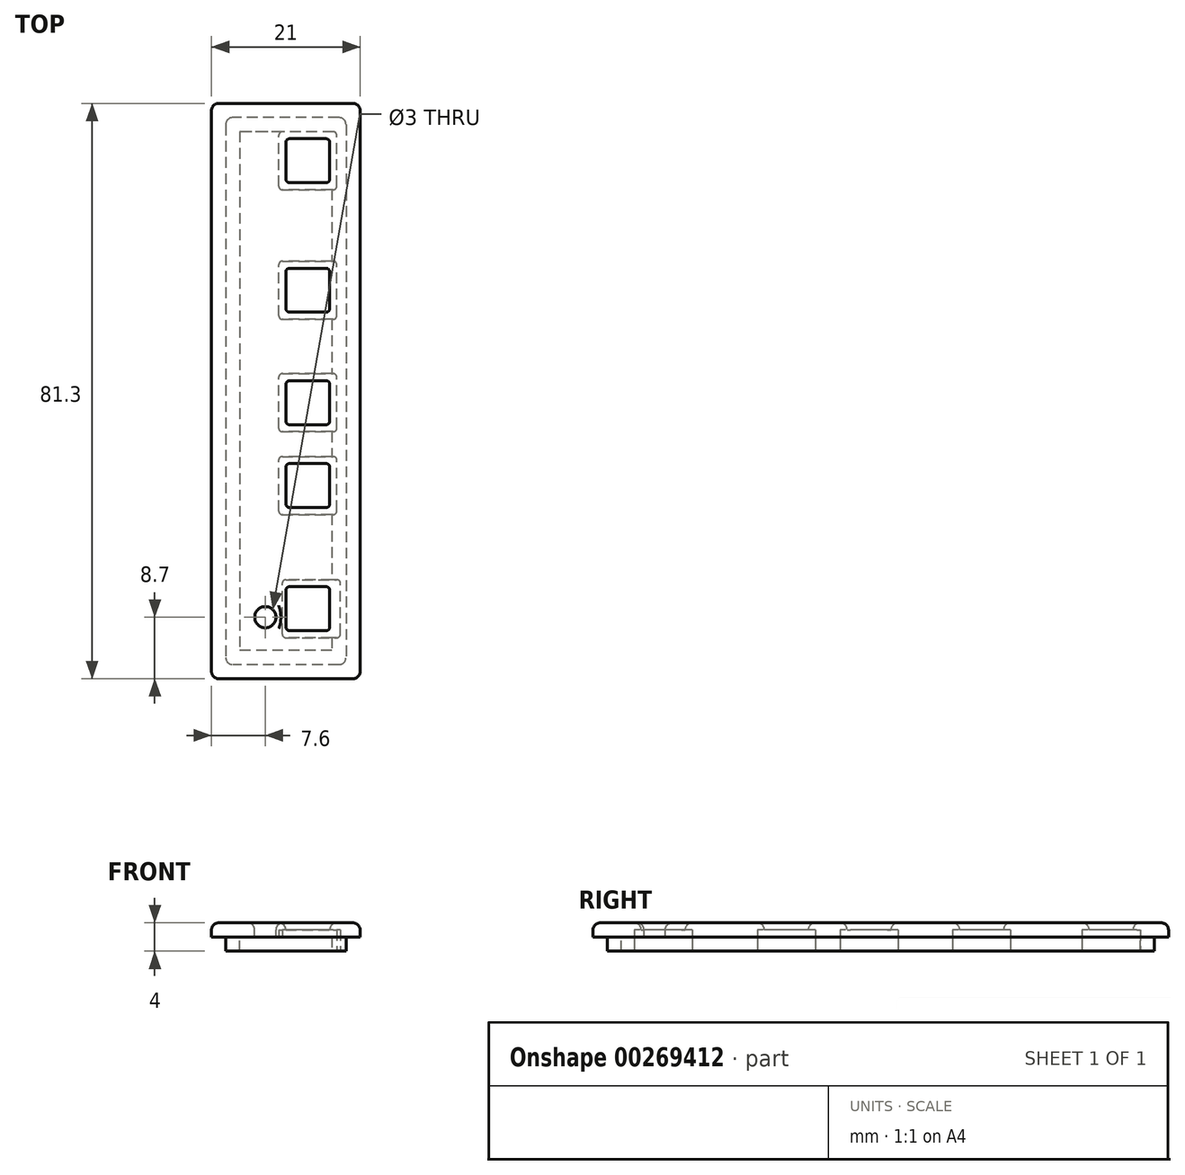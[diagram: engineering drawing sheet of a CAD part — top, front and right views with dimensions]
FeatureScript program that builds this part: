
annotation { "Feature Type Name" : "Feature", "Feature Type Description" : "" }
export const myFeature = defineFeature(function(context is Context, id is Id, definition is map)
    precondition{}
    {
        {
            var Q0;
            Q0=qCreatedBy(makeId("Top.planeOp"),FACE);
            var sketch = newSketch(context, id + "F0", { "sketchPlane" : qUnion([Q0])});
            skLineSegment(sketch, "E0.bottom", {"start": v(8.5, 38.65) * mm, "end": v(-8.5, 38.65) * mm});
            skLineSegment(sketch, "E0.top", {"start": v(8.5, -38.65) * mm, "end": v(-8.5, -38.65) * mm});
            skLineSegment(sketch, "E0.left", {"start": v(8.5, 38.65) * mm, "end": v(8.5, -38.65) * mm});
            skLineSegment(sketch, "E0.right", {"start": v(-8.5, 38.65) * mm, "end": v(-8.5, -38.65) * mm});
            skPoint(sketch, "E0.middle", {"position": v(0, 0) * mm});
            skLineSegment(sketch, "E1.0", {"start": v(10.5, 40.65) * mm, "end": v(-10.5, 40.65) * mm});
            skLineSegment(sketch, "E1.1", {"start": v(10.5, 40.65) * mm, "end": v(10.5, -40.65) * mm});
            skLineSegment(sketch, "E1.2", {"start": v(10.5, -40.65) * mm, "end": v(-10.5, -40.65) * mm});
            skLineSegment(sketch, "E1.3", {"start": v(-10.5, 40.65) * mm, "end": v(-10.5, -40.65) * mm});
            skLineSegment(sketch, "E2.0", {"start": v(6.5, 36.65) * mm, "end": v(-6.5, 36.65) * mm});
            skLineSegment(sketch, "E2.1", {"start": v(6.5, 36.65) * mm, "end": v(6.5, -36.65) * mm});
            skLineSegment(sketch, "E2.2", {"start": v(6.5, -36.65) * mm, "end": v(-6.5, -36.65) * mm});
            skLineSegment(sketch, "E2.3", {"start": v(-6.5, 36.65) * mm, "end": v(-6.5, -36.65) * mm});
            skSolve(sketch);
        }
        {
            var Q0;
            Q0=makeQuery(id+"F0.imprint","IMPRINT",FACE,{"disambiguationData":[TD([[makeQuery(id+"F0.imprint","IMPRINT",EDGE,{"derivedFrom":sQuery(id+"F0.wireOp",EDGE,"E2.0")}),1.0]])]});
            var Q1;
            Q1=makeQuery(id+"F0.imprint","IMPRINT",FACE,{"disambiguationData":[TD([[makeQuery(id+"F0.imprint","IMPRINT",EDGE,{"derivedFrom":sQuery(id+"F0.wireOp",EDGE,"E0.bottom")}),1.0]])]});
            var Q2;
            Q2=makeQuery(id+"F0.imprint","IMPRINT",FACE,{"disambiguationData":[TD([[makeQuery(id+"F0.imprint","IMPRINT",EDGE,{"derivedFrom":sQuery(id+"F0.wireOp",EDGE,"E0.bottom")}),-1.0]])]});
            extrude(context, id + "F1", {"entities" : qUnion([Q0, Q1, Q2]), "depth" : 2 * mm});
        }
        {
            var Q0;
            Q0=makeQuery(id+"F0.imprint","IMPRINT",FACE,{"disambiguationData":[TD([[makeQuery(id+"F0.imprint","IMPRINT",EDGE,{"derivedFrom":sQuery(id+"F0.wireOp",EDGE,"E0.bottom")}),1.0]])]});
            extrude(context, id + "F2", {"entities" : qUnion([Q0]), "operationType" : NewBodyOperationType.ADD, "oppositeDirection" : true, "depth" : 2 * mm});
        }
        {
            var Q0;
            Q0=makeQuery(id+"F1.opExtrude","CAP_FACE",FACE,{"disambiguationData":[OSD([sQuery(id+"F0.wireOp",EDGE,"E1.0"),sQuery(id+"F0.wireOp",EDGE,"E1.1"),sQuery(id+"F0.wireOp",EDGE,"E1.2"),sQuery(id+"F0.wireOp",EDGE,"E1.3")])],"isStart":false});
            var sketch = newSketch(context, id + "F3", { "sketchPlane" : qUnion([Q0])});
            skLineSegment(sketch, "E3.bottom", {"start": v(5.7, 35.65) * mm, "end": v(0.5, 35.65) * mm});
            skLineSegment(sketch, "E3.top", {"start": v(5.7, 29.45) * mm, "end": v(0.5, 29.45) * mm});
            skLineSegment(sketch, "E3.left", {"start": v(6.2, 35.15) * mm, "end": v(6.2, 29.95) * mm});
            skLineSegment(sketch, "E3.right", {"start": v(0, 35.15) * mm, "end": v(0, 29.95) * mm});
            skLineSegment(sketch, "E4.bottom", {"start": v(5.7, 17.35) * mm, "end": v(0.5, 17.35) * mm});
            skLineSegment(sketch, "E4.top", {"start": v(5.7, 11.15) * mm, "end": v(0.5, 11.15) * mm});
            skLineSegment(sketch, "E4.left", {"start": v(6.2, 16.85) * mm, "end": v(6.2, 11.65) * mm});
            skLineSegment(sketch, "E4.right", {"start": v(0, 16.85) * mm, "end": v(0, 11.65) * mm});
            skLineSegment(sketch, "E5.bottom", {"start": v(0.5, 1.45) * mm, "end": v(5.7, 1.45) * mm});
            skLineSegment(sketch, "E5.top", {"start": v(0.5, -4.75) * mm, "end": v(5.7, -4.75) * mm});
            skLineSegment(sketch, "E5.left", {"start": v(0, 0.95) * mm, "end": v(0, -4.25) * mm});
            skLineSegment(sketch, "E5.right", {"start": v(6.2, 0.95) * mm, "end": v(6.2, -4.25) * mm});
            skLineSegment(sketch, "E6.bottom", {"start": v(5.7, -10.25) * mm, "end": v(0.5, -10.25) * mm});
            skLineSegment(sketch, "E6.top", {"start": v(5.7, -16.45) * mm, "end": v(0.5, -16.45) * mm});
            skLineSegment(sketch, "E6.left", {"start": v(6.2, -10.75) * mm, "end": v(6.2, -15.95) * mm});
            skLineSegment(sketch, "E6.right", {"start": v(0, -10.75) * mm, "end": v(0, -15.95) * mm});
            skLineSegment(sketch, "E7.bottom", {"start": v(5.7, -27.65) * mm, "end": v(0.5, -27.65) * mm});
            skLineSegment(sketch, "E7.top", {"start": v(5.7, -33.85) * mm, "end": v(0.5, -33.85) * mm});
            skLineSegment(sketch, "E7.left", {"start": v(6.2, -28.15) * mm, "end": v(6.2, -33.35) * mm});
            skLineSegment(sketch, "E7.right", {"start": v(0, -28.15) * mm, "end": v(0, -33.35) * mm});
            skPoint(sketch, "E8.visualSharp", {"position": v(6.2, 17.35) * mm});
            skArc(sketch, "E8.filletArc", {"start": v(6.2, 16.85) * mm, "mid": v(6.05, 17.2) * mm, "end": v(5.7, 17.35) * mm});
            skPoint(sketch, "E9.visualSharp", {"position": v(0, 17.35) * mm});
            skArc(sketch, "E9.filletArc", {"start": v(0.5, 17.35) * mm, "mid": v(0.15, 17.2) * mm, "end": v(0, 16.85) * mm});
            skPoint(sketch, "E10.visualSharp", {"position": v(0, 11.15) * mm});
            skArc(sketch, "E10.filletArc", {"start": v(0, 11.65) * mm, "mid": v(0.15, 11.3) * mm, "end": v(0.5, 11.15) * mm});
            skPoint(sketch, "E11.visualSharp", {"position": v(6.2, 11.15) * mm});
            skArc(sketch, "E11.filletArc", {"start": v(5.7, 11.15) * mm, "mid": v(6.05, 11.3) * mm, "end": v(6.2, 11.65) * mm});
            skPoint(sketch, "E12.visualSharp", {"position": v(6.2, 29.45) * mm});
            skArc(sketch, "E12.filletArc", {"start": v(5.7, 29.45) * mm, "mid": v(6.05, 29.6) * mm, "end": v(6.2, 29.95) * mm});
            skPoint(sketch, "E13.visualSharp", {"position": v(6.2, 35.65) * mm});
            skArc(sketch, "E13.filletArc", {"start": v(6.2, 35.15) * mm, "mid": v(6.05, 35.5) * mm, "end": v(5.7, 35.65) * mm});
            skPoint(sketch, "E14.visualSharp", {"position": v(0, 35.65) * mm});
            skArc(sketch, "E14.filletArc", {"start": v(0.5, 35.65) * mm, "mid": v(0.15, 35.5) * mm, "end": v(0, 35.15) * mm});
            skPoint(sketch, "E15.visualSharp", {"position": v(0, 29.45) * mm});
            skArc(sketch, "E15.filletArc", {"start": v(0, 29.95) * mm, "mid": v(0.15, 29.6) * mm, "end": v(0.5, 29.45) * mm});
            skPoint(sketch, "E16.visualSharp", {"position": v(0, 1.45) * mm});
            skArc(sketch, "E16.filletArc", {"start": v(0.5, 1.45) * mm, "mid": v(0.15, 1.3) * mm, "end": v(0, 0.95) * mm});
            skPoint(sketch, "E17.visualSharp", {"position": v(0, -4.75) * mm});
            skArc(sketch, "E17.filletArc", {"start": v(0, -4.25) * mm, "mid": v(0.15, -4.6) * mm, "end": v(0.5, -4.75) * mm});
            skPoint(sketch, "E18.visualSharp", {"position": v(6.2, 1.45) * mm});
            skArc(sketch, "E18.filletArc", {"start": v(6.2, 0.95) * mm, "mid": v(6.05, 1.3) * mm, "end": v(5.7, 1.45) * mm});
            skPoint(sketch, "E19.visualSharp", {"position": v(6.2, -4.75) * mm});
            skArc(sketch, "E19.filletArc", {"start": v(5.7, -4.75) * mm, "mid": v(6.05, -4.6) * mm, "end": v(6.2, -4.25) * mm});
            skPoint(sketch, "E20.visualSharp", {"position": v(0, -10.25) * mm});
            skArc(sketch, "E20.filletArc", {"start": v(0.5, -10.25) * mm, "mid": v(0.15, -10.4) * mm, "end": v(0, -10.75) * mm});
            skPoint(sketch, "E21.visualSharp", {"position": v(0, -16.45) * mm});
            skArc(sketch, "E21.filletArc", {"start": v(0, -15.95) * mm, "mid": v(0.15, -16.3) * mm, "end": v(0.5, -16.45) * mm});
            skPoint(sketch, "E22.visualSharp", {"position": v(6.2, -16.45) * mm});
            skArc(sketch, "E22.filletArc", {"start": v(5.7, -16.45) * mm, "mid": v(6.05, -16.3) * mm, "end": v(6.2, -15.95) * mm});
            skPoint(sketch, "E23.visualSharp", {"position": v(6.2, -10.25) * mm});
            skArc(sketch, "E23.filletArc", {"start": v(6.2, -10.75) * mm, "mid": v(6.05, -10.4) * mm, "end": v(5.7, -10.25) * mm});
            skPoint(sketch, "E24.visualSharp", {"position": v(0, -27.65) * mm});
            skArc(sketch, "E24.filletArc", {"start": v(0.5, -27.65) * mm, "mid": v(0.15, -27.8) * mm, "end": v(0, -28.15) * mm});
            skPoint(sketch, "E25.visualSharp", {"position": v(0, -33.85) * mm});
            skArc(sketch, "E25.filletArc", {"start": v(0, -33.35) * mm, "mid": v(0.15, -33.7) * mm, "end": v(0.5, -33.85) * mm});
            skPoint(sketch, "E26.visualSharp", {"position": v(6.2, -33.85) * mm});
            skArc(sketch, "E26.filletArc", {"start": v(5.7, -33.85) * mm, "mid": v(6.05, -33.7) * mm, "end": v(6.2, -33.35) * mm});
            skPoint(sketch, "E27.visualSharp", {"position": v(6.2, -27.65) * mm});
            skArc(sketch, "E27.filletArc", {"start": v(6.2, -28.15) * mm, "mid": v(6.05, -27.8) * mm, "end": v(5.7, -27.65) * mm});
            skCircle(sketch, "E28", {"center": v(-2.9, -31.95) * mm, "radius": 1.5 * mm});
            skSolve(sketch);
        }
        {
            var Q0;
            Q0=makeQuery(id+"F3.imprint","IMPRINT",FACE,{"disambiguationData":[TD([[makeQuery(id+"F3.imprint","IMPRINT",EDGE,{"derivedFrom":sQuery(id+"F3.wireOp",EDGE,"E3.bottom")}),1.0]])]});
            var Q1;
            Q1=makeQuery(id+"F3.imprint","IMPRINT",FACE,{"disambiguationData":[TD([[makeQuery(id+"F3.imprint","IMPRINT",EDGE,{"derivedFrom":sQuery(id+"F3.wireOp",EDGE,"E4.bottom")}),1.0]])]});
            var Q2;
            Q2=makeQuery(id+"F3.imprint","IMPRINT",FACE,{"disambiguationData":[TD([[makeQuery(id+"F3.imprint","IMPRINT",EDGE,{"derivedFrom":sQuery(id+"F3.wireOp",EDGE,"E5.bottom")}),-1.0]])]});
            var Q3;
            Q3=makeQuery(id+"F3.imprint","IMPRINT",FACE,{"disambiguationData":[TD([[makeQuery(id+"F3.imprint","IMPRINT",EDGE,{"derivedFrom":sQuery(id+"F3.wireOp",EDGE,"E6.bottom")}),1.0]])]});
            var Q4;
            Q4=makeQuery(id+"F3.imprint","IMPRINT",FACE,{"disambiguationData":[TD([[makeQuery(id+"F3.imprint","IMPRINT",EDGE,{"derivedFrom":sQuery(id+"F3.wireOp",EDGE,"E7.bottom")}),1.0]])]});
            var Q5;
            Q5=makeQuery(id+"F3.imprint","IMPRINT",FACE,{"disambiguationData":[TD([[makeQuery(id+"F3.imprint","IMPRINT",EDGE,{"derivedFrom":sQuery(id+"F3.wireOp",EDGE,"E28")}),1.0]])]});
            extrude(context, id + "F4", {"entities" : qUnion([Q0, Q1, Q2, Q3, Q4, Q5]), "operationType" : NewBodyOperationType.REMOVE, "oppositeDirection" : true, "depth" : 25 * mm});
        }
        {
            var Q0;
            Q0=makeQuery(id+"F1.opExtrude","CAP_FACE",FACE,{"disambiguationData":[OSD([sQuery(id+"F0.wireOp",EDGE,"E1.0"),sQuery(id+"F0.wireOp",EDGE,"E1.1"),sQuery(id+"F0.wireOp",EDGE,"E1.2"),sQuery(id+"F0.wireOp",EDGE,"E1.3")])],"isStart":false});
            var Q1;
            Q1=makeQuery(id+"F1.opExtrude","SWEPT_EDGE",EDGE,{"disambiguationData":[OSD([sQuery(id+"F0.wireOp",EDGE,"E1.1"),sQuery(id+"F0.wireOp",EDGE,"E1.2")])]});
            var Q2;
            Q2=makeQuery(id+"F1.opExtrude","SWEPT_EDGE",EDGE,{"disambiguationData":[OSD([sQuery(id+"F0.wireOp",EDGE,"E1.2"),sQuery(id+"F0.wireOp",EDGE,"E1.3")])]});
            var Q3;
            Q3=makeQuery(id+"F1.opExtrude","SWEPT_EDGE",EDGE,{"disambiguationData":[OSD([sQuery(id+"F0.wireOp",EDGE,"E1.0"),sQuery(id+"F0.wireOp",EDGE,"E1.3")])]});
            var Q4;
            Q4=makeQuery(id+"F1.opExtrude","SWEPT_EDGE",EDGE,{"disambiguationData":[OSD([sQuery(id+"F0.wireOp",EDGE,"E1.0"),sQuery(id+"F0.wireOp",EDGE,"E1.1")])]});
            var Q5;
            Q5=makeQuery(id+"F2.opExtrude","SWEPT_EDGE",EDGE,{"disambiguationData":[OSD([sQuery(id+"F0.wireOp",EDGE,"E0.bottom"),sQuery(id+"F0.wireOp",EDGE,"E0.left")])]});
            var Q6;
            Q6=makeQuery(id+"F2.opExtrude","SWEPT_EDGE",EDGE,{"disambiguationData":[OSD([sQuery(id+"F0.wireOp",EDGE,"E0.bottom"),sQuery(id+"F0.wireOp",EDGE,"E0.right")])]});
            var Q7;
            Q7=makeQuery(id+"F2.opExtrude","SWEPT_EDGE",EDGE,{"disambiguationData":[OSD([sQuery(id+"F0.wireOp",EDGE,"E0.top"),sQuery(id+"F0.wireOp",EDGE,"E0.left")])]});
            var Q8;
            Q8=makeQuery(id+"F2.opExtrude","SWEPT_EDGE",EDGE,{"disambiguationData":[OSD([sQuery(id+"F0.wireOp",EDGE,"E0.top"),sQuery(id+"F0.wireOp",EDGE,"E0.right")])]});
            fillet(context, id + "F5", {"entities" : qUnion([Q0, Q1, Q2, Q3, Q4, Q5, Q6, Q7, Q8]), "radius" : 1 * mm, "tangentPropagation" : true, "allowEdgeOverflow" : false});
        }
        {
            var Q0;
            Q0=makeQuery(id+"F0.imprint","IMPRINT",FACE,{"disambiguationData":[TD([[makeQuery(id+"F0.imprint","IMPRINT",EDGE,{"derivedFrom":sQuery(id+"F0.wireOp",EDGE,"E2.0")}),1.0]])]});
            var sketch = newSketch(context, id + "F6", { "sketchPlane" : qUnion([Q0])});
            skLineSegment(sketch, "E29.bottom", {"start": v(0, -26.65) * mm, "end": v(7.2, -26.65) * mm});
            skLineSegment(sketch, "E29.top", {"start": v(0, -34.85) * mm, "end": v(7.2, -34.85) * mm});
            skLineSegment(sketch, "E29.left", {"start": v(-0.5, -27.15) * mm, "end": v(-0.5, -34.35) * mm});
            skLineSegment(sketch, "E29.right", {"start": v(7.7, -27.15) * mm, "end": v(7.7, -34.35) * mm});
            skPoint(sketch, "E29.middle", {"position": v(3.6, -30.75) * mm});
            skLineSegment(sketch, "E30.bottom", {"start": v(-0.5, 36.65) * mm, "end": v(6.7, 36.65) * mm});
            skLineSegment(sketch, "E30.top", {"start": v(-0.5, 28.45) * mm, "end": v(6.7, 28.45) * mm});
            skLineSegment(sketch, "E30.left", {"start": v(-1, 36.15) * mm, "end": v(-1, 28.95) * mm});
            skLineSegment(sketch, "E30.right", {"start": v(7.2, 36.15) * mm, "end": v(7.2, 28.95) * mm});
            skPoint(sketch, "E30.middle", {"position": v(3.1, 32.55) * mm});
            skLineSegment(sketch, "E31.bottom", {"start": v(-0.5, 18.35) * mm, "end": v(6.7, 18.35) * mm});
            skLineSegment(sketch, "E31.top", {"start": v(-0.5, 10.15) * mm, "end": v(6.7, 10.15) * mm});
            skLineSegment(sketch, "E31.left", {"start": v(-1, 17.85) * mm, "end": v(-1, 10.65) * mm});
            skLineSegment(sketch, "E31.right", {"start": v(7.2, 17.85) * mm, "end": v(7.2, 10.65) * mm});
            skPoint(sketch, "E31.middle", {"position": v(3.1, 14.25) * mm});
            skLineSegment(sketch, "E32.bottom", {"start": v(-0.5, 2.45) * mm, "end": v(6.7, 2.45) * mm});
            skLineSegment(sketch, "E32.top", {"start": v(-0.5, -5.75) * mm, "end": v(6.7, -5.75) * mm});
            skLineSegment(sketch, "E32.left", {"start": v(-1, 1.95) * mm, "end": v(-1, -5.25) * mm});
            skLineSegment(sketch, "E32.right", {"start": v(7.2, 1.95) * mm, "end": v(7.2, -5.25) * mm});
            skPoint(sketch, "E32.middle", {"position": v(3.1, -1.65) * mm});
            skLineSegment(sketch, "E33.bottom", {"start": v(-0.5, -9.25) * mm, "end": v(6.7, -9.25) * mm});
            skLineSegment(sketch, "E33.top", {"start": v(-0.5, -17.45) * mm, "end": v(6.7, -17.45) * mm});
            skLineSegment(sketch, "E33.left", {"start": v(-1, -9.75) * mm, "end": v(-1, -16.95) * mm});
            skLineSegment(sketch, "E33.right", {"start": v(7.2, -9.75) * mm, "end": v(7.2, -16.95) * mm});
            skPoint(sketch, "E33.middle", {"position": v(3.1, -13.35) * mm});
            skPoint(sketch, "E34.visualSharp", {"position": v(7.2, -9.25) * mm});
            skArc(sketch, "E34.filletArc", {"start": v(7.2, -9.75) * mm, "mid": v(7.05, -9.4) * mm, "end": v(6.7, -9.25) * mm});
            skPoint(sketch, "E35.visualSharp", {"position": v(7.2, -17.45) * mm});
            skArc(sketch, "E35.filletArc", {"start": v(6.7, -17.45) * mm, "mid": v(7.05, -17.3) * mm, "end": v(7.2, -16.95) * mm});
            skPoint(sketch, "E36.visualSharp", {"position": v(-1, -17.45) * mm});
            skArc(sketch, "E36.filletArc", {"start": v(-1, -16.95) * mm, "mid": v(-0.85, -17.3) * mm, "end": v(-0.5, -17.45) * mm});
            skPoint(sketch, "E37.visualSharp", {"position": v(-1, -9.25) * mm});
            skArc(sketch, "E37.filletArc", {"start": v(-0.5, -9.25) * mm, "mid": v(-0.85, -9.4) * mm, "end": v(-1, -9.75) * mm});
            skPoint(sketch, "E38.visualSharp", {"position": v(7.2, -5.75) * mm});
            skArc(sketch, "E38.filletArc", {"start": v(6.7, -5.75) * mm, "mid": v(7.05, -5.6) * mm, "end": v(7.2, -5.25) * mm});
            skPoint(sketch, "E39.visualSharp", {"position": v(-1, -5.75) * mm});
            skArc(sketch, "E39.filletArc", {"start": v(-1, -5.25) * mm, "mid": v(-0.85, -5.6) * mm, "end": v(-0.5, -5.75) * mm});
            skPoint(sketch, "E40.visualSharp", {"position": v(-1, 2.45) * mm});
            skArc(sketch, "E40.filletArc", {"start": v(-0.5, 2.45) * mm, "mid": v(-0.85, 2.3) * mm, "end": v(-1, 1.95) * mm});
            skPoint(sketch, "E41.visualSharp", {"position": v(7.2, 2.45) * mm});
            skArc(sketch, "E41.filletArc", {"start": v(7.2, 1.95) * mm, "mid": v(7.05, 2.3) * mm, "end": v(6.7, 2.45) * mm});
            skPoint(sketch, "E42.visualSharp", {"position": v(7.2, 18.35) * mm});
            skArc(sketch, "E42.filletArc", {"start": v(7.2, 17.85) * mm, "mid": v(7.05, 18.2) * mm, "end": v(6.7, 18.35) * mm});
            skPoint(sketch, "E43.visualSharp", {"position": v(7.2, 10.15) * mm});
            skArc(sketch, "E43.filletArc", {"start": v(6.7, 10.15) * mm, "mid": v(7.05, 10.3) * mm, "end": v(7.2, 10.65) * mm});
            skPoint(sketch, "E44.visualSharp", {"position": v(-1, 10.15) * mm});
            skArc(sketch, "E44.filletArc", {"start": v(-1, 10.65) * mm, "mid": v(-0.85, 10.3) * mm, "end": v(-0.5, 10.15) * mm});
            skPoint(sketch, "E45.visualSharp", {"position": v(-1, 18.35) * mm});
            skArc(sketch, "E45.filletArc", {"start": v(-0.5, 18.35) * mm, "mid": v(-0.85, 18.2) * mm, "end": v(-1, 17.85) * mm});
            skPoint(sketch, "E46.visualSharp", {"position": v(7.2, 36.65) * mm});
            skArc(sketch, "E46.filletArc", {"start": v(7.2, 36.15) * mm, "mid": v(7.05, 36.5) * mm, "end": v(6.7, 36.65) * mm});
            skPoint(sketch, "E47.visualSharp", {"position": v(7.2, 28.45) * mm});
            skArc(sketch, "E47.filletArc", {"start": v(6.7, 28.45) * mm, "mid": v(7.05, 28.6) * mm, "end": v(7.2, 28.95) * mm});
            skPoint(sketch, "E48.visualSharp", {"position": v(-1, 28.45) * mm});
            skArc(sketch, "E48.filletArc", {"start": v(-1, 28.95) * mm, "mid": v(-0.85, 28.6) * mm, "end": v(-0.5, 28.45) * mm});
            skPoint(sketch, "E49.visualSharp", {"position": v(-1, 36.65) * mm});
            skArc(sketch, "E49.filletArc", {"start": v(-0.5, 36.65) * mm, "mid": v(-0.85, 36.5) * mm, "end": v(-1, 36.15) * mm});
            skPoint(sketch, "E50.visualSharp", {"position": v(7.7, -26.65) * mm});
            skArc(sketch, "E50.filletArc", {"start": v(7.7, -27.15) * mm, "mid": v(7.55, -26.8) * mm, "end": v(7.2, -26.65) * mm});
            skPoint(sketch, "E51.visualSharp", {"position": v(7.7, -34.85) * mm});
            skArc(sketch, "E51.filletArc", {"start": v(7.2, -34.85) * mm, "mid": v(7.55, -34.7) * mm, "end": v(7.7, -34.35) * mm});
            skPoint(sketch, "E52.visualSharp", {"position": v(-0.5, -34.85) * mm});
            skArc(sketch, "E52.filletArc", {"start": v(-0.5, -34.35) * mm, "mid": v(-0.35, -34.7) * mm, "end": v(0, -34.85) * mm});
            skPoint(sketch, "E53.visualSharp", {"position": v(-0.5, -26.65) * mm});
            skArc(sketch, "E53.filletArc", {"start": v(0, -26.65) * mm, "mid": v(-0.35, -26.8) * mm, "end": v(-0.5, -27.15) * mm});
            skSolve(sketch);
        }
        {
            var Q0;
            Q0=makeQuery(id+"F6.imprint","IMPRINT",FACE,{"disambiguationData":[TD([[makeQuery(id+"F6.imprint","IMPRINT",EDGE,{"derivedFrom":sQuery(id+"F6.wireOp",EDGE,"E29.left")}),1.0]])]});
            var Q1;
            Q1=makeQuery(id+"F6.imprint","IMPRINT",FACE,{"disambiguationData":[TD([[makeQuery(id+"F6.imprint","IMPRINT",EDGE,{"derivedFrom":sQuery(id+"F6.wireOp",EDGE,"E29.right")}),-1.0]])]});
            var Q2;
            Q2=makeQuery(id+"F6.imprint","IMPRINT",FACE,{"disambiguationData":[TD([[makeQuery(id+"F6.imprint","IMPRINT",EDGE,{"derivedFrom":sQuery(id+"F6.wireOp",EDGE,"E33.left")}),1.0]])]});
            var Q3;
            Q3=makeQuery(id+"F6.imprint","IMPRINT",FACE,{"disambiguationData":[TD([[makeQuery(id+"F6.imprint","IMPRINT",EDGE,{"derivedFrom":sQuery(id+"F6.wireOp",EDGE,"E33.right")}),-1.0]])]});
            var Q4;
            Q4=makeQuery(id+"F6.imprint","IMPRINT",FACE,{"disambiguationData":[TD([[makeQuery(id+"F6.imprint","IMPRINT",EDGE,{"derivedFrom":sQuery(id+"F6.wireOp",EDGE,"E32.left")}),1.0]])]});
            var Q5;
            Q5=makeQuery(id+"F6.imprint","IMPRINT",FACE,{"disambiguationData":[TD([[makeQuery(id+"F6.imprint","IMPRINT",EDGE,{"derivedFrom":sQuery(id+"F6.wireOp",EDGE,"E32.right")}),-1.0]])]});
            var Q6;
            Q6=makeQuery(id+"F6.imprint","IMPRINT",FACE,{"disambiguationData":[TD([[makeQuery(id+"F6.imprint","IMPRINT",EDGE,{"derivedFrom":sQuery(id+"F6.wireOp",EDGE,"E31.left")}),1.0]])]});
            var Q7;
            Q7=makeQuery(id+"F6.imprint","IMPRINT",FACE,{"disambiguationData":[TD([[makeQuery(id+"F6.imprint","IMPRINT",EDGE,{"derivedFrom":sQuery(id+"F6.wireOp",EDGE,"E31.right")}),-1.0]])]});
            var Q8;
            {var subQ1=sQuery(id+"F6.wireOp",EDGE,"E30.left");Q8=makeQuery(id+"F6.imprint","IMPRINT",FACE,{"disambiguationData":[TD([[makeQuery(id+"F6.imprint","IMPRINT",EDGE,{"derivedFrom":subQ1}),1.0]])]});}
            var Q9;
            Q9=makeQuery(id+"F6.imprint","IMPRINT",FACE,{"disambiguationData":[TD([[makeQuery(id+"F6.imprint","IMPRINT",EDGE,{"derivedFrom":sQuery(id+"F6.wireOp",EDGE,"E30.bottom")}),-1.0]])]});
            extrude(context, id + "F7", {"entities" : qUnion([Q0, Q1, Q2, Q3, Q4, Q5, Q6, Q7, Q8, Q9]), "operationType" : NewBodyOperationType.REMOVE, "depth" : 1 * mm, "hasSecondDirection" : true, "secondDirectionOppositeDirection" : true, "secondDirectionDepth" : 3 * mm});
        }
    });
